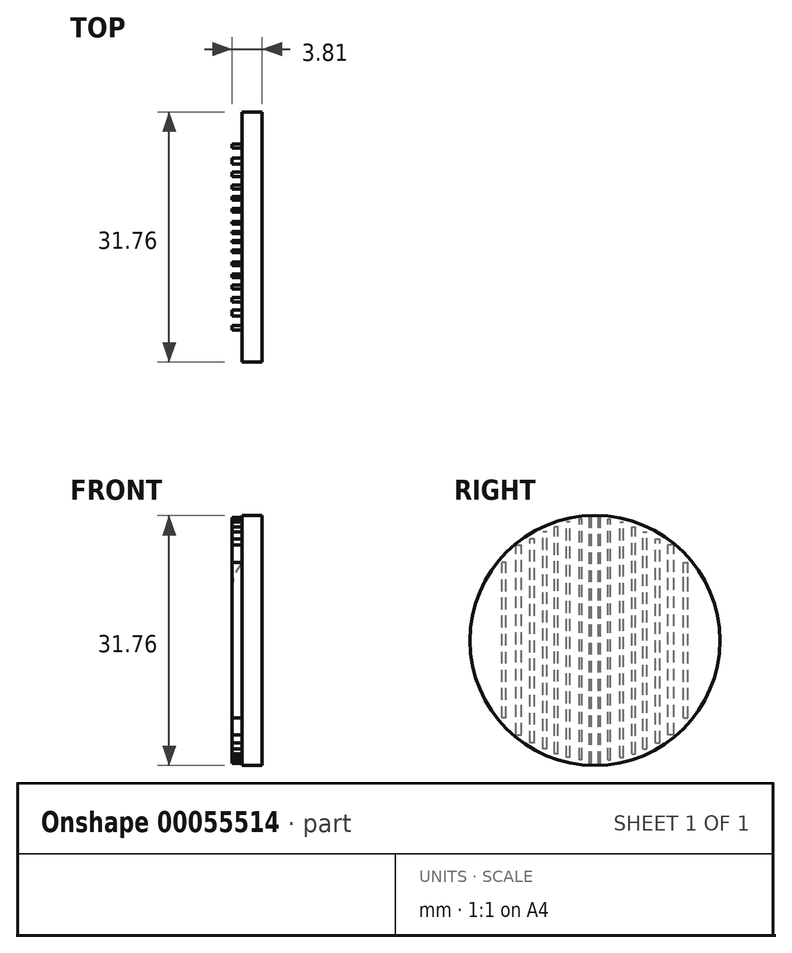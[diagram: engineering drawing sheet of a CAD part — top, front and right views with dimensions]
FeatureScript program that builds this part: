
annotation { "Feature Type Name" : "Feature", "Feature Type Description" : "" }
export const myFeature = defineFeature(function(context is Context, id is Id, definition is map)
    precondition{}
    {
        {
            var Q0;
            Q0=qCreatedBy(makeId("Right.planeOp"),FACE);
            var sketch = newSketch(context, id + "F0", { "sketchPlane" : qUnion([Q0])});
            skCircle(sketch, "E0", {"center": v(0, 0) * mm, "radius": 15.88 * mm});
            skSolve(sketch);
        }
        {
            var Q0;
            Q0 = qSketchRegion(id + "F0", true);
            extrude(context, id + "F1", {"entities" : qUnion([Q0]), "depth" : 2.54 * mm});
        }
        {
            var Q0;
            Q0=qCreatedBy(makeId("Right.planeOp"),FACE);
            var sketch = newSketch(context, id + "F2", { "sketchPlane" : qUnion([Q0])});
            skLineSegment(sketch, "E1", {"start": v(0, -16) * mm, "end": v(0, 15.82) * mm, "construction": true});
            skLineSegment(sketch, "E2.bottom", {"start": v(-0.46, -15.58) * mm, "end": v(-0.7, -15.58) * mm});
            skLineSegment(sketch, "E2.top", {"start": v(-0.46, 15.61) * mm, "end": v(-0.7, 15.61) * mm});
            skLineSegment(sketch, "E2.left", {"start": v(-0.46, -15.58) * mm, "end": v(-0.46, 15.61) * mm});
            skLineSegment(sketch, "E2.right", {"start": v(-0.7, -15.58) * mm, "end": v(-0.7, 15.61) * mm});
            skLineSegment(sketch, "E3.bottom", {"start": v(-1.63, -15.16) * mm, "end": v(-1.96, -15.16) * mm});
            skLineSegment(sketch, "E3.top", {"start": v(-1.63, 15.44) * mm, "end": v(-1.96, 15.44) * mm});
            skLineSegment(sketch, "E3.left", {"start": v(-1.63, -15.16) * mm, "end": v(-1.63, 15.44) * mm});
            skLineSegment(sketch, "E3.right", {"start": v(-1.96, -15.16) * mm, "end": v(-1.96, 15.44) * mm});
            skLineSegment(sketch, "E4.bottom", {"start": v(-3.18, -14.87) * mm, "end": v(-3.64, -14.87) * mm});
            skLineSegment(sketch, "E4.top", {"start": v(-3.18, 15.07) * mm, "end": v(-3.64, 15.07) * mm});
            skLineSegment(sketch, "E4.left", {"start": v(-3.18, -14.87) * mm, "end": v(-3.18, 15.07) * mm});
            skLineSegment(sketch, "E4.right", {"start": v(-3.64, -14.87) * mm, "end": v(-3.64, 15.07) * mm});
            skLineSegment(sketch, "E5.bottom", {"start": v(-4.69, -14.4) * mm, "end": v(-5.15, -14.4) * mm});
            skLineSegment(sketch, "E5.top", {"start": v(-4.69, 14.44) * mm, "end": v(-5.15, 14.44) * mm});
            skLineSegment(sketch, "E5.left", {"start": v(-4.69, -14.4) * mm, "end": v(-4.69, 14.44) * mm});
            skLineSegment(sketch, "E5.right", {"start": v(-5.15, -14.4) * mm, "end": v(-5.15, 14.44) * mm});
            skLineSegment(sketch, "E6.bottom", {"start": v(-6.12, -13.78) * mm, "end": v(-6.62, -13.78) * mm});
            skLineSegment(sketch, "E6.top", {"start": v(-6.12, 13.77) * mm, "end": v(-6.62, 13.77) * mm});
            skLineSegment(sketch, "E6.left", {"start": v(-6.12, -13.78) * mm, "end": v(-6.12, 13.77) * mm});
            skLineSegment(sketch, "E6.right", {"start": v(-6.62, -13.78) * mm, "end": v(-6.62, 13.77) * mm});
            skLineSegment(sketch, "E7.bottom", {"start": v(-7.7, -12.98) * mm, "end": v(-8.25, -12.98) * mm});
            skLineSegment(sketch, "E7.top", {"start": v(-7.7, 12.93) * mm, "end": v(-8.25, 12.93) * mm});
            skLineSegment(sketch, "E7.left", {"start": v(-7.7, -12.98) * mm, "end": v(-7.7, 12.93) * mm});
            skLineSegment(sketch, "E7.right", {"start": v(-8.25, -12.98) * mm, "end": v(-8.25, 12.93) * mm});
            skLineSegment(sketch, "E8.bottom", {"start": v(-10.06, -11.97) * mm, "end": v(-9.3, -11.97) * mm});
            skLineSegment(sketch, "E8.top", {"start": v(-10.06, 12.13) * mm, "end": v(-9.3, 12.13) * mm});
            skLineSegment(sketch, "E8.left", {"start": v(-10.06, -11.97) * mm, "end": v(-10.06, 12.13) * mm});
            skLineSegment(sketch, "E8.right", {"start": v(-9.3, -11.97) * mm, "end": v(-9.3, 12.13) * mm});
            skLineSegment(sketch, "E9.bottom", {"start": v(-11.27, -9.84) * mm, "end": v(-11.82, -9.84) * mm});
            skLineSegment(sketch, "E9.top", {"start": v(-11.27, 9.9) * mm, "end": v(-11.82, 9.9) * mm});
            skLineSegment(sketch, "E9.left", {"start": v(-11.27, -9.84) * mm, "end": v(-11.27, 9.9) * mm});
            skLineSegment(sketch, "E9.right", {"start": v(-11.82, -9.84) * mm, "end": v(-11.82, 9.9) * mm});
            skLineSegment(sketch, "E10.MirrorCS", {"start": v(0.46, -15.58) * mm, "end": v(0.46, 15.61) * mm});
            skLineSegment(sketch, "E11.MirrorCS", {"start": v(0.46, 15.61) * mm, "end": v(0.7, 15.61) * mm});
            skLineSegment(sketch, "E12.MirrorCS", {"start": v(0.46, -15.58) * mm, "end": v(0.7, -15.58) * mm});
            skLineSegment(sketch, "E13.MirrorCS", {"start": v(11.27, -9.84) * mm, "end": v(11.82, -9.84) * mm});
            skLineSegment(sketch, "E14.MirrorCS", {"start": v(1.63, 15.44) * mm, "end": v(1.96, 15.44) * mm});
            skLineSegment(sketch, "E15.MirrorCS", {"start": v(1.63, -15.16) * mm, "end": v(1.96, -15.16) * mm});
            skLineSegment(sketch, "E16.MirrorCS", {"start": v(3.18, -14.87) * mm, "end": v(3.64, -14.87) * mm});
            skLineSegment(sketch, "E17.MirrorCS", {"start": v(3.18, 15.07) * mm, "end": v(3.64, 15.07) * mm});
            skLineSegment(sketch, "E18.MirrorCS", {"start": v(4.69, 14.44) * mm, "end": v(5.15, 14.44) * mm});
            skLineSegment(sketch, "E19.MirrorCS", {"start": v(10.06, -11.97) * mm, "end": v(9.3, -11.97) * mm});
            skLineSegment(sketch, "E20.MirrorCS", {"start": v(7.7, 12.93) * mm, "end": v(8.25, 12.93) * mm});
            skLineSegment(sketch, "E21.MirrorCS", {"start": v(4.69, -14.4) * mm, "end": v(5.15, -14.4) * mm});
            skLineSegment(sketch, "E22.MirrorCS", {"start": v(10.06, 12.13) * mm, "end": v(9.3, 12.13) * mm});
            skLineSegment(sketch, "E23.MirrorCS", {"start": v(6.12, 13.77) * mm, "end": v(6.62, 13.77) * mm});
            skLineSegment(sketch, "E24.MirrorCS", {"start": v(6.12, -13.78) * mm, "end": v(6.62, -13.78) * mm});
            skLineSegment(sketch, "E25.MirrorCS", {"start": v(7.7, -12.98) * mm, "end": v(8.25, -12.98) * mm});
            skLineSegment(sketch, "E26.MirrorCS", {"start": v(11.27, 9.9) * mm, "end": v(11.82, 9.9) * mm});
            skLineSegment(sketch, "E27.MirrorCS", {"start": v(10.06, -11.97) * mm, "end": v(10.06, 12.13) * mm});
            skLineSegment(sketch, "E28.MirrorCS", {"start": v(7.7, -12.98) * mm, "end": v(7.7, 12.93) * mm});
            skLineSegment(sketch, "E29.MirrorCS", {"start": v(6.62, -13.78) * mm, "end": v(6.62, 13.77) * mm});
            skLineSegment(sketch, "E30.MirrorCS", {"start": v(11.82, -9.84) * mm, "end": v(11.82, 9.9) * mm});
            skLineSegment(sketch, "E31.MirrorCS", {"start": v(1.63, -15.16) * mm, "end": v(1.63, 15.44) * mm});
            skLineSegment(sketch, "E32.MirrorCS", {"start": v(0.7, -15.58) * mm, "end": v(0.7, 15.61) * mm});
            skLineSegment(sketch, "E33.MirrorCS", {"start": v(1.96, -15.16) * mm, "end": v(1.96, 15.44) * mm});
            skLineSegment(sketch, "E34.MirrorCS", {"start": v(5.15, -14.4) * mm, "end": v(5.15, 14.44) * mm});
            skLineSegment(sketch, "E35.MirrorCS", {"start": v(3.18, -14.87) * mm, "end": v(3.18, 15.07) * mm});
            skLineSegment(sketch, "E36.MirrorCS", {"start": v(4.69, -14.4) * mm, "end": v(4.69, 14.44) * mm});
            skLineSegment(sketch, "E37.MirrorCS", {"start": v(3.64, -14.87) * mm, "end": v(3.64, 15.07) * mm});
            skLineSegment(sketch, "E38.MirrorCS", {"start": v(11.27, -9.84) * mm, "end": v(11.27, 9.9) * mm});
            skLineSegment(sketch, "E39.MirrorCS", {"start": v(6.12, -13.78) * mm, "end": v(6.12, 13.77) * mm});
            skLineSegment(sketch, "E40.MirrorCS", {"start": v(8.25, -12.98) * mm, "end": v(8.25, 12.93) * mm});
            skLineSegment(sketch, "E41.MirrorCS", {"start": v(9.3, -11.97) * mm, "end": v(9.3, 12.13) * mm});
            skSolve(sketch);
        }
        {
            var Q0;
            Q0=makeQuery(id+"F2.imprint","IMPRINT",FACE,{"disambiguationData":[TD([[makeQuery(id+"F2.imprint","IMPRINT",EDGE,{"derivedFrom":sQuery(id+"F2.wireOp",EDGE,"E2.bottom")}),-1.0]])]});
            var Q1;
            Q1=makeQuery(id+"F2.imprint","IMPRINT",FACE,{"disambiguationData":[TD([[makeQuery(id+"F2.imprint","IMPRINT",EDGE,{"derivedFrom":sQuery(id+"F2.wireOp",EDGE,"E3.bottom")}),-1.0]])]});
            var Q2;
            Q2=makeQuery(id+"F2.imprint","IMPRINT",FACE,{"disambiguationData":[TD([[makeQuery(id+"F2.imprint","IMPRINT",EDGE,{"derivedFrom":sQuery(id+"F2.wireOp",EDGE,"E4.bottom")}),-1.0]])]});
            var Q3;
            Q3=makeQuery(id+"F2.imprint","IMPRINT",FACE,{"disambiguationData":[TD([[makeQuery(id+"F2.imprint","IMPRINT",EDGE,{"derivedFrom":sQuery(id+"F2.wireOp",EDGE,"E5.bottom")}),-1.0]])]});
            var Q4;
            Q4=makeQuery(id+"F2.imprint","IMPRINT",FACE,{"disambiguationData":[TD([[makeQuery(id+"F2.imprint","IMPRINT",EDGE,{"derivedFrom":sQuery(id+"F2.wireOp",EDGE,"E6.bottom")}),-1.0]])]});
            var Q5;
            Q5=makeQuery(id+"F2.imprint","IMPRINT",FACE,{"disambiguationData":[TD([[makeQuery(id+"F2.imprint","IMPRINT",EDGE,{"derivedFrom":sQuery(id+"F2.wireOp",EDGE,"E7.bottom")}),-1.0]])]});
            var Q6;
            Q6=makeQuery(id+"F2.imprint","IMPRINT",FACE,{"disambiguationData":[TD([[makeQuery(id+"F2.imprint","IMPRINT",EDGE,{"derivedFrom":sQuery(id+"F2.wireOp",EDGE,"E8.bottom")}),1.0]])]});
            var Q7;
            Q7=makeQuery(id+"F2.imprint","IMPRINT",FACE,{"disambiguationData":[TD([[makeQuery(id+"F2.imprint","IMPRINT",EDGE,{"derivedFrom":sQuery(id+"F2.wireOp",EDGE,"E9.bottom")}),-1.0]])]});
            var Q8;
            Q8=makeQuery(id+"F2.imprint","IMPRINT",FACE,{"disambiguationData":[TD([[makeQuery(id+"F2.imprint","IMPRINT",EDGE,{"derivedFrom":sQuery(id+"F2.wireOp",EDGE,"E11.MirrorCS")}),-1.0]])]});
            var Q9;
            Q9=makeQuery(id+"F2.imprint","IMPRINT",FACE,{"disambiguationData":[TD([[makeQuery(id+"F2.imprint","IMPRINT",EDGE,{"derivedFrom":sQuery(id+"F2.wireOp",EDGE,"E13.MirrorCS")}),1.0]])]});
            var Q10;
            Q10=makeQuery(id+"F2.imprint","IMPRINT",FACE,{"disambiguationData":[TD([[makeQuery(id+"F2.imprint","IMPRINT",EDGE,{"derivedFrom":sQuery(id+"F2.wireOp",EDGE,"E14.MirrorCS")}),-1.0]])]});
            var Q11;
            Q11=makeQuery(id+"F2.imprint","IMPRINT",FACE,{"disambiguationData":[TD([[makeQuery(id+"F2.imprint","IMPRINT",EDGE,{"derivedFrom":sQuery(id+"F2.wireOp",EDGE,"E16.MirrorCS")}),1.0]])]});
            var Q12;
            Q12=makeQuery(id+"F2.imprint","IMPRINT",FACE,{"disambiguationData":[TD([[makeQuery(id+"F2.imprint","IMPRINT",EDGE,{"derivedFrom":sQuery(id+"F2.wireOp",EDGE,"E18.MirrorCS")}),-1.0]])]});
            var Q13;
            Q13=makeQuery(id+"F2.imprint","IMPRINT",FACE,{"disambiguationData":[TD([[makeQuery(id+"F2.imprint","IMPRINT",EDGE,{"derivedFrom":sQuery(id+"F2.wireOp",EDGE,"E19.MirrorCS")}),-1.0]])]});
            var Q14;
            Q14=makeQuery(id+"F2.imprint","IMPRINT",FACE,{"disambiguationData":[TD([[makeQuery(id+"F2.imprint","IMPRINT",EDGE,{"derivedFrom":sQuery(id+"F2.wireOp",EDGE,"E20.MirrorCS")}),-1.0]])]});
            var Q15;
            Q15=makeQuery(id+"F2.imprint","IMPRINT",FACE,{"disambiguationData":[TD([[makeQuery(id+"F2.imprint","IMPRINT",EDGE,{"derivedFrom":sQuery(id+"F2.wireOp",EDGE,"E23.MirrorCS")}),-1.0]])]});
            extrude(context, id + "F3", {"entities" : qUnion([Q0, Q1, Q2, Q3, Q4, Q5, Q6, Q7, Q8, Q9, Q10, Q11, Q12, Q13, Q14, Q15]), "operationType" : NewBodyOperationType.ADD, "oppositeDirection" : true, "depth" : 1.27 * mm});
        }
        {
            var Q0;
            Q0=makeQuery(id+"F3.opExtrude","CAP_EDGE",EDGE,{"disambiguationData":[OSD([sQuery(id+"F2.wireOp",EDGE,"E26.MirrorCS")])],"isStart":false});
            fillet(context, id + "F4", {"entities" : qUnion([Q0]), "radius" : 5.08 * mm, "tangentPropagation" : true, "allowEdgeOverflow" : false});
        }
    });
